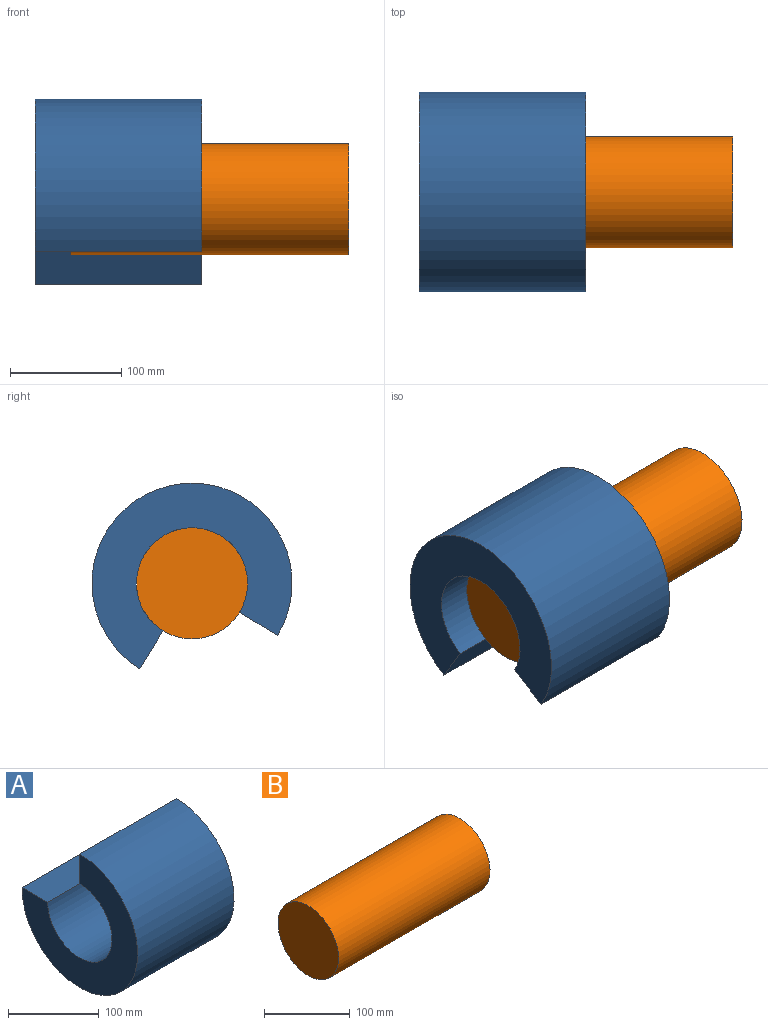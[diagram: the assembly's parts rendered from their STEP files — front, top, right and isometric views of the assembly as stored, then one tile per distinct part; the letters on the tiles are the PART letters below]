
ASSEMBLY  parts=2 mates=1
PART A: 6 faces, bbox 150x180x180 mm
  f0: cylinder r=90mm len=180mm, axis (-1,0,0), area 63617.3mm2, adj f1,f3,f4,f5
  f1: plane 180x180mm, normal (-1,0,0), area 13194.7mm2, adj f0,f2,f4,f5
  f2: cylinder r=50mm len=150mm, axis (-1,0,0), area 35342.9mm2, adj f1,f3,f4,f5
  f3: plane 180x180mm, normal (1,0,0), area 13194.7mm2, adj f0,f2,f4,f5
  f4: plane 150x40mm, normal (0,0,1), area 6000mm2, adj f0,f1,f2,f3
  f5: plane 150x40mm, normal (0,1,0), area 6000mm2, adj f0,f1,f2,f3
PART B: 3 faces, bbox 250x100x100 mm
  f0: cylinder r=50mm len=250mm, axis (1,0,0), area 78539.8mm2, adj f1,f2
  f1: plane 100x100mm, normal (-1,0,0), area 7854mm2, adj f0
  f2: plane 100x100mm, normal (1,0,0), area 7854mm2, adj f0
PLACE A rot(axis=(-1,0,0),148.6deg) t=(-197.16,-41.42,9.08)mm
PLACE B t=(-81.23,-41.42,9.08)mm fixed
MATE cylindrical B.f0 <-> A.f0  axis (1,0,0) through (-82.23,-41.42,9.08)mm
